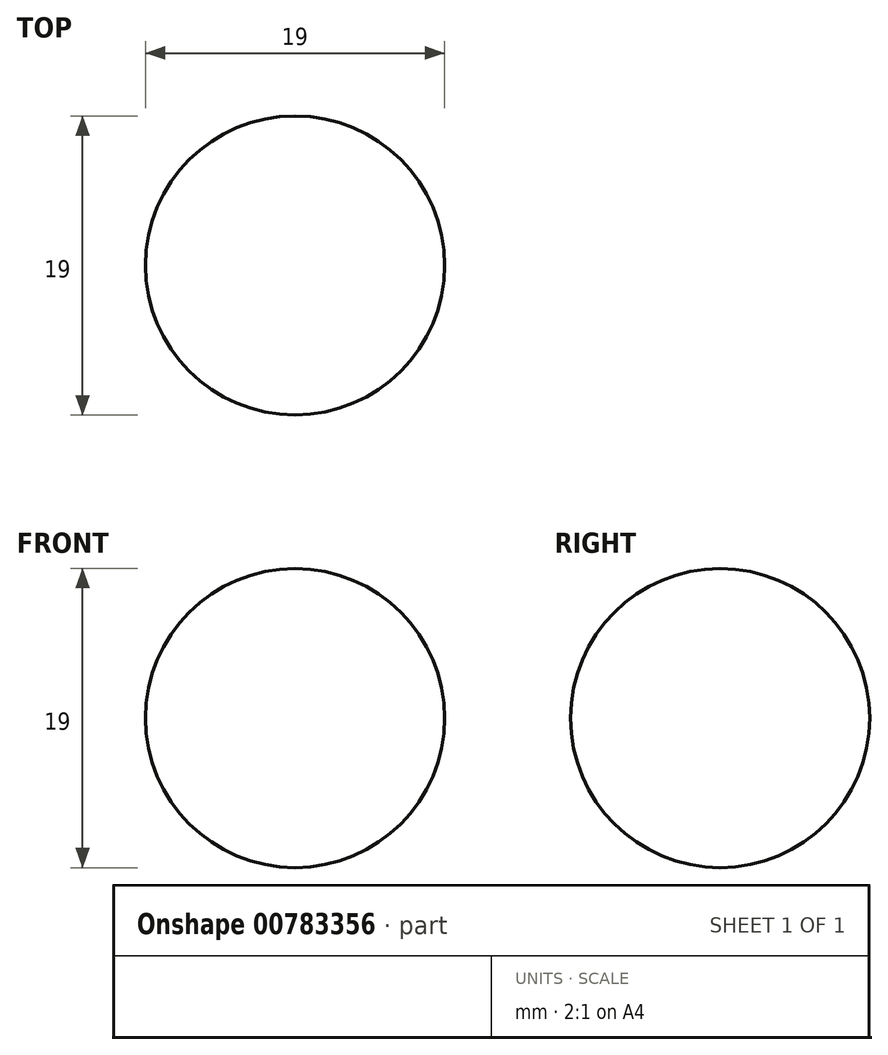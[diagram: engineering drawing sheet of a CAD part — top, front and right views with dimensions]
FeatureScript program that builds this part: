
annotation { "Feature Type Name" : "Feature", "Feature Type Description" : "" }
export const myFeature = defineFeature(function(context is Context, id is Id, definition is map)
    precondition{}
    {
        {
            var Q0;
            Q0=qCreatedBy(makeId("Top.planeOp"),FACE);
            var sketch = newSketch(context, id + "F0", { "sketchPlane" : qUnion([Q0])});
            skCircle(sketch, "E0", {"center": v(0, 0) * mm, "radius": 9.5 * mm});
            skLineSegment(sketch, "E1", {"start": v(-9.5, 0) * mm, "end": v(9.5, 0) * mm});
            skSolve(sketch);
        }
        {
            var Q0;
            {var subQ0=sQuery(id+"F0.wireOp",EDGE,"E1");Q0=makeQuery(id+"F0.imprint","IMPRINT",FACE,{"disambiguationData":[TD([[makeQuery(id+"F0.imprint","IMPRINT",EDGE,{"derivedFrom":subQ0}),-1.0]])]});}
            var Q1;
            Q1=sQuery(id+"F0.wireOp",EDGE,"E1");
            revolve(context, id + "F1", {"surfaceOperationType" : NewSurfaceOperationType.NEW, "entities" : qUnion([Q0]), "axis" : qUnion([Q1]), "revolveType" : RevolveType.FULL});
        }
    });
